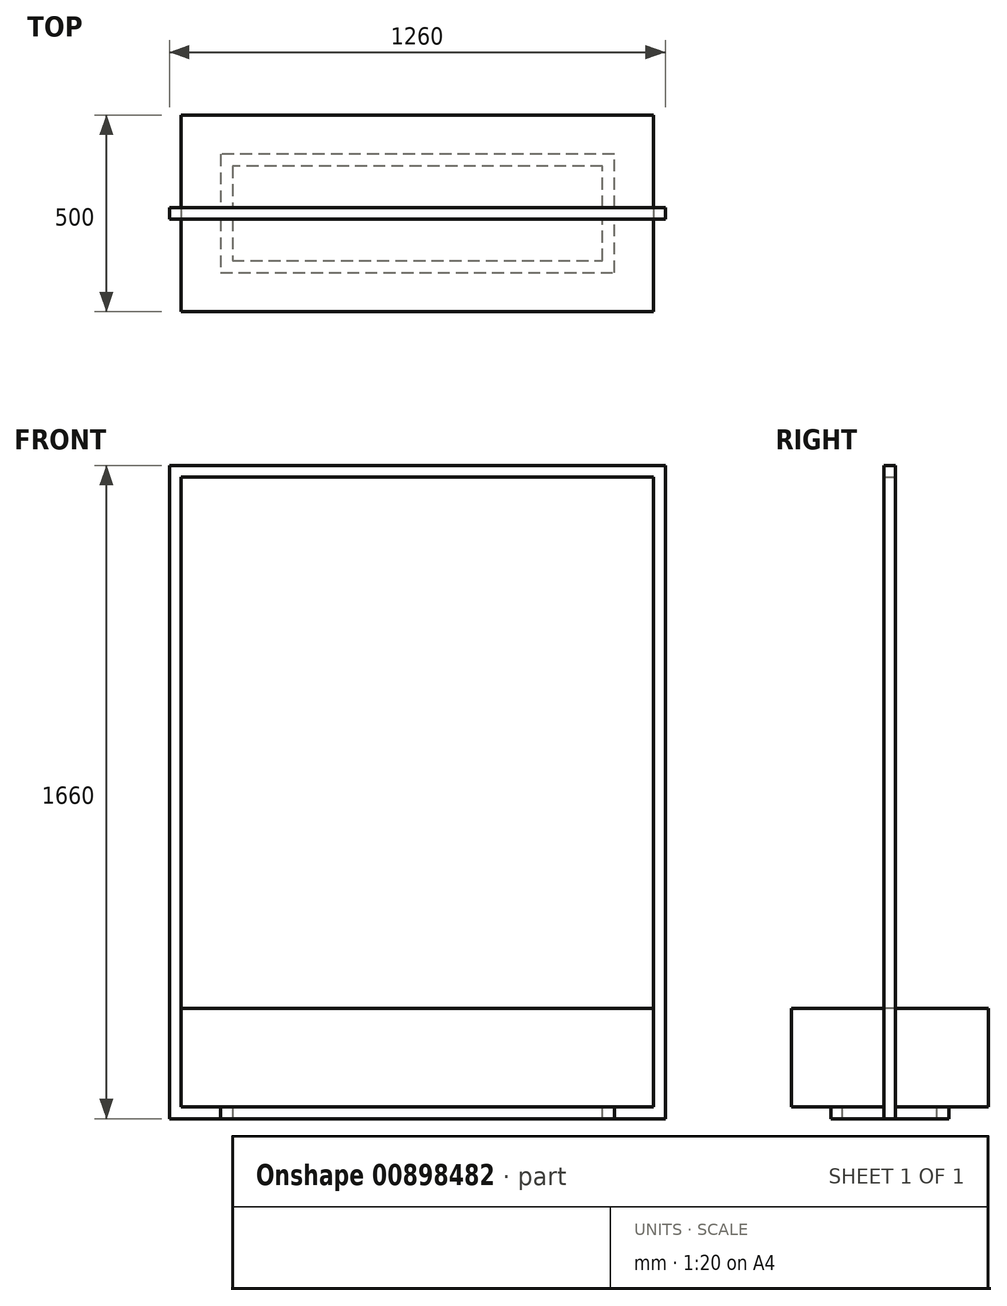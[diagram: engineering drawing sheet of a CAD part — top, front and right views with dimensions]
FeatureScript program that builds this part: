
annotation { "Feature Type Name" : "Feature", "Feature Type Description" : "" }
export const myFeature = defineFeature(function(context is Context, id is Id, definition is map)
    precondition{}
    {
        {
            var Q0;
            Q0=qCreatedBy(makeId("Top.planeOp"),FACE);
            var sketch = newSketch(context, id + "F0", { "sketchPlane" : qUnion([Q0])});
            skLineSegment(sketch, "E0.bottom", {"start": v(-600, 250) * mm, "end": v(600, 250) * mm});
            skLineSegment(sketch, "E0.top", {"start": v(-600, -250) * mm, "end": v(600, -250) * mm});
            skLineSegment(sketch, "E0.left", {"start": v(-600, 250) * mm, "end": v(-600, -250) * mm});
            skLineSegment(sketch, "E0.right", {"start": v(600, 250) * mm, "end": v(600, -250) * mm});
            skLineSegment(sketch, "E1", {"start": v(-600, 250) * mm, "end": v(600, -250) * mm, "construction": true});
            skSolve(sketch);
        }
        {
            var Q0;
            Q0 = qSketchRegion(id + "F0", true);
            extrude(context, id + "F1", {"entities" : qUnion([Q0]), "depth" : 250 * mm, "offsetDistance" : 25 * mm});
        }
        {
            var Q0;
            Q0=qCreatedBy(makeId("Front.planeOp"),FACE);
            var sketch = newSketch(context, id + "F2", { "sketchPlane" : qUnion([Q0])});
            skLineSegment(sketch, "E2", {"start": v(600, 0) * mm, "end": v(600, 1600) * mm});
            skLineSegment(sketch, "E3", {"start": v(600, 1600) * mm, "end": v(-600, 1600) * mm});
            skLineSegment(sketch, "E4", {"start": v(-600, 1600) * mm, "end": v(-600, 0) * mm});
            skLineSegment(sketch, "E5", {"start": v(-600, 0) * mm, "end": v(600, 0) * mm});
            skLineSegment(sketch, "E6.0", {"start": v(630, 1630) * mm, "end": v(-630, 1630) * mm});
            skLineSegment(sketch, "E6.1", {"start": v(630, -30) * mm, "end": v(630, 1630) * mm});
            skLineSegment(sketch, "E6.2", {"start": v(-630, -30) * mm, "end": v(630, -30) * mm});
            skLineSegment(sketch, "E6.3", {"start": v(-630, 1630) * mm, "end": v(-630, -30) * mm});
            skSolve(sketch);
        }
        {
            var Q0;
            Q0 = qSketchRegion(id + "F2", true);
            extrude(context, id + "F3", {"entities" : qUnion([Q0]), "endBound" : BoundingType.SYMMETRIC, "depth" : 30 * mm, "offsetDistance" : 25 * mm});
        }
        {
            var Q0;
            Q0=makeQuery(id+"F1.opExtrude","CAP_FACE",FACE,{"disambiguationData":[OSD([sQuery(id+"F0.wireOp",EDGE,"E0.bottom"),sQuery(id+"F0.wireOp",EDGE,"E0.top"),sQuery(id+"F0.wireOp",EDGE,"E0.left"),sQuery(id+"F0.wireOp",EDGE,"E0.right")])],"isStart":true});
            var sketch = newSketch(context, id + "F4", { "sketchPlane" : qUnion([Q0])});
            skLineSegment(sketch, "E7", {"start": v(500, 150) * mm, "end": v(500, -150) * mm});
            skLineSegment(sketch, "E8", {"start": v(500, -150) * mm, "end": v(-500, -150) * mm});
            skLineSegment(sketch, "E9", {"start": v(-500, -150) * mm, "end": v(-500, 150) * mm});
            skLineSegment(sketch, "E10", {"start": v(-500, 150) * mm, "end": v(500, 150) * mm});
            skLineSegment(sketch, "E11.0", {"start": v(-470, 120) * mm, "end": v(470, 120) * mm});
            skLineSegment(sketch, "E11.1", {"start": v(-470, -120) * mm, "end": v(-470, 120) * mm});
            skLineSegment(sketch, "E11.2", {"start": v(470, -120) * mm, "end": v(-470, -120) * mm});
            skLineSegment(sketch, "E11.3", {"start": v(470, 120) * mm, "end": v(470, -120) * mm});
            skSolve(sketch);
        }
        {
            var Q0;
            Q0 = qSketchRegion(id + "F4", true);
            extrude(context, id + "F5", {"entities" : qUnion([Q0]), "operationType" : NewBodyOperationType.ADD, "depth" : 30 * mm, "offsetDistance" : 25 * mm});
        }
    });
